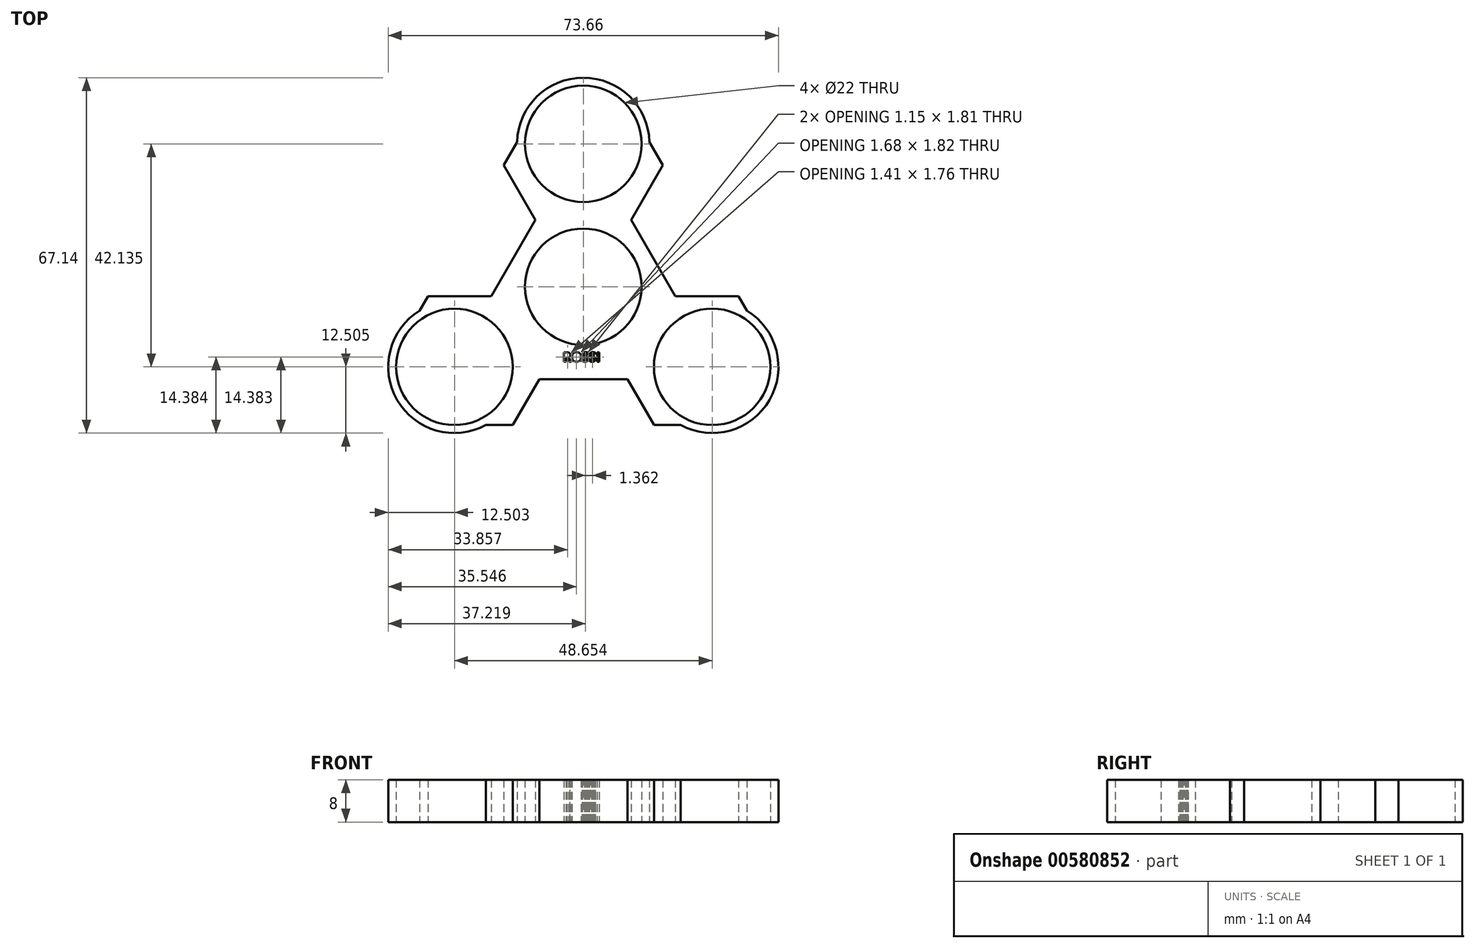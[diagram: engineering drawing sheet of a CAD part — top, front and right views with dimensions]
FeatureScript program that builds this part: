
annotation { "Feature Type Name" : "Feature", "Feature Type Description" : "" }
export const myFeature = defineFeature(function(context is Context, id is Id, definition is map)
    precondition{}
    {
        {
            var Q0;
            Q0=qCreatedBy(makeId("Top.planeOp"),FACE);
            var sketch = newSketch(context, id + "F0", { "sketchPlane" : qUnion([Q0])});
            skCircle(sketch, "E0", {"center": v(0, 0) * mm, "radius": 11 * mm});
            skCircle(sketch, "E1", {"center": v(0, 27) * mm, "radius": 11 * mm});
            skCircle(sketch, "E2.1.0", {"center": v(-24.33, -15.14) * mm, "radius": 11 * mm});
            skCircle(sketch, "E2.2.0", {"center": v(24.33, -15.14) * mm, "radius": 11 * mm});
            skPoint(sketch, "E2.center", {"position": v(0, -1.1) * mm});
            skLineSegment(sketch, "E3", {"start": v(-9.53, 32.5) * mm, "end": v(-15.03, 22.97) * mm});
            skLineSegment(sketch, "E4", {"start": v(-24.33, -26.14) * mm, "end": v(-13.33, -26.14) * mm});
            skLineSegment(sketch, "E5", {"start": v(9.53, 32.5) * mm, "end": v(15.03, 22.97) * mm});
            skLineSegment(sketch, "E6", {"start": v(-13.33, -26.14) * mm, "end": v(-8.33, -17.48) * mm});
            skLineSegment(sketch, "E7", {"start": v(13.33, -26.14) * mm, "end": v(8.33, -17.47) * mm});
            skLineSegment(sketch, "E8", {"start": v(-8.33, -17.48) * mm, "end": v(8.33, -17.48) * mm});
            skLineSegment(sketch, "E9.1.0", {"start": v(17.38, -1.79) * mm, "end": v(9.06, 12.63) * mm});
            skLineSegment(sketch, "E9.1.1", {"start": v(27.38, -1.79) * mm, "end": v(17.38, -1.79) * mm});
            skLineSegment(sketch, "E9.1.2", {"start": v(14.06, 21.3) * mm, "end": v(9.06, 12.63) * mm});
            skLineSegment(sketch, "E9.2.0", {"start": v(-9.06, 12.63) * mm, "end": v(-17.38, -1.79) * mm});
            skLineSegment(sketch, "E9.2.1", {"start": v(-14.06, 21.3) * mm, "end": v(-9.06, 12.63) * mm});
            skLineSegment(sketch, "E9.2.2", {"start": v(-27.38, -1.79) * mm, "end": v(-17.38, -1.79) * mm});
            skPoint(sketch, "E9.center", {"position": v(0, -2.2) * mm});
            skLineSegment(sketch, "E10", {"start": v(-25.16, -1.79) * mm, "end": v(-29.32, -1.79) * mm});
            skLineSegment(sketch, "E11", {"start": v(17.38, -1.79) * mm, "end": v(29.32, -1.79) * mm});
            skLineSegment(sketch, "E12", {"start": v(9.06, 12.63) * mm, "end": v(15.03, 22.97) * mm});
            skLineSegment(sketch, "E13", {"start": v(-9.06, 12.63) * mm, "end": v(-15.03, 22.97) * mm});
            skLineSegment(sketch, "E14.trimOffspring", {"start": v(-29.32, -1.79) * mm, "end": v(-33.85, -9.64) * mm});
            skLineSegment(sketch, "E15.trimOffspring", {"start": v(29.32, -1.79) * mm, "end": v(33.85, -9.64) * mm});
            skLineSegment(sketch, "E16.trimOffspring", {"start": v(13.33, -26.14) * mm, "end": v(24.33, -26.14) * mm});
            skCircle(sketch, "E17", {"center": v(24.33, -15.14) * mm, "radius": 12.5 * mm});
            skCircle(sketch, "E18", {"center": v(-24.33, -15.14) * mm, "radius": 12.5 * mm});
            skCircle(sketch, "E19", {"center": v(0, 27) * mm, "radius": 12.5 * mm});
            skText(sketch, "E20", { "text": "ROSSI\n", "fontName": "OpenSans-Bold.ttf"});
            const initialGuessF0  = {"E20": [-0.0039, -0.01414, 1, 0, 0.00178]};
            skSetInitialGuess(sketch, initialGuessF0);
            skSolve(sketch);
        }
        {
            var Q0;
            Q0 = qSketchRegion(id + "F0", true);
            extrude(context, id + "F1", {"entities" : qUnion([Q0]), "depth" : 8 * mm, "offsetDistance" : 25 * mm});
        }
    });
